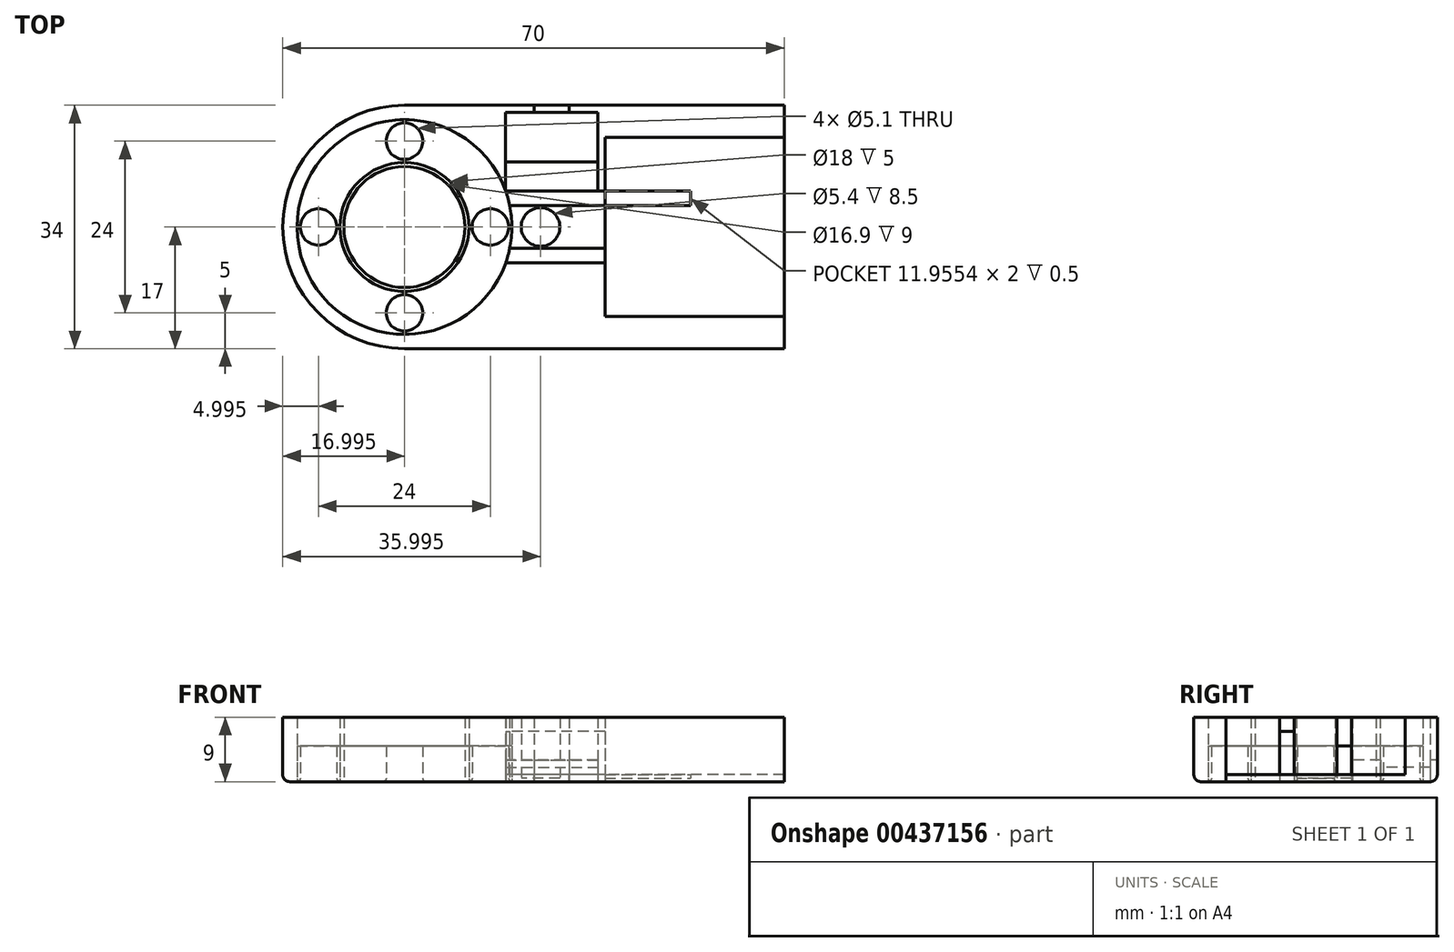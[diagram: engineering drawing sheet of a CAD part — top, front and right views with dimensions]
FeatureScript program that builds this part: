
annotation { "Feature Type Name" : "Feature", "Feature Type Description" : "" }
export const myFeature = defineFeature(function(context is Context, id is Id, definition is map)
    precondition{}
    {
        {
            var Q0;
            Q0=qCreatedBy(makeId("Top.planeOp"),FACE);
            var sketch = newSketch(context, id + "F0", { "sketchPlane" : qUnion([Q0])});
            skPoint(sketch, "E0", {"position": v(-7.91, 0) * mm});
            skPoint(sketch, "E1", {"position": v(33.09, 0) * mm});
            skLineSegment(sketch, "E2", {"start": v(-7.91, 17) * mm, "end": v(45.09, 17) * mm});
            skLineSegment(sketch, "E3", {"start": v(45.09, 17) * mm, "end": v(45.09, -17) * mm});
            skLineSegment(sketch, "E4", {"start": v(45.09, -17) * mm, "end": v(-7.91, -17) * mm});
            skArc(sketch, "E5", {"start": v(-7.91, -17) * mm, "mid": v(-24.91, 0) * mm, "end": v(-7.91, 17) * mm});
            skCircle(sketch, "E6", {"center": v(-7.91, 0) * mm, "radius": 8.45 * mm});
            skLineSegment(sketch, "E7", {"start": v(45.09, 12.5) * mm, "end": v(20.09, 12.5) * mm});
            skLineSegment(sketch, "E8", {"start": v(20.09, 12.5) * mm, "end": v(20.09, -12.5) * mm});
            skLineSegment(sketch, "E9", {"start": v(20.09, -12.5) * mm, "end": v(45.09, -12.5) * mm});
            skCircle(sketch, "E10", {"center": v(-7.91, 0) * mm, "radius": 9 * mm});
            skCircle(sketch, "E11", {"center": v(-7.91, 0) * mm, "radius": 15 * mm});
            skCircle(sketch, "E12", {"center": v(-7.91, 12) * mm, "radius": 2.55 * mm});
            skCircle(sketch, "E13", {"center": v(-7.91, -12) * mm, "radius": 2.55 * mm});
            skCircle(sketch, "E14", {"center": v(4.09, 0) * mm, "radius": 2.55 * mm});
            skCircle(sketch, "E15", {"center": v(-19.91, 0) * mm, "radius": 2.55 * mm});
            skCircle(sketch, "E16", {"center": v(11.09, 0) * mm, "radius": 2.7 * mm});
            skLineSegment(sketch, "E17", {"start": v(20.09, 3) * mm, "end": v(6.78, 3) * mm});
            skLineSegment(sketch, "E18", {"start": v(20.09, 5) * mm, "end": v(6.23, 5) * mm});
            skLineSegment(sketch, "E19", {"start": v(20.09, -3) * mm, "end": v(6.78, -3) * mm});
            skLineSegment(sketch, "E20", {"start": v(20.09, -5) * mm, "end": v(6.23, -5) * mm});
            skLineSegment(sketch, "E21.bottom", {"start": v(6.19, 16) * mm, "end": v(19.09, 16) * mm});
            skLineSegment(sketch, "E21.left", {"start": v(6.19, 16) * mm, "end": v(6.19, 6) * mm});
            skLineSegment(sketch, "E21.right", {"start": v(19.09, 16) * mm, "end": v(19.09, 6) * mm});
            skLineSegment(sketch, "E22", {"start": v(6.19, 9.1) * mm, "end": v(19.09, 9.1) * mm});
            skLineSegment(sketch, "E23", {"start": v(10.19, 17) * mm, "end": v(10.19, 16) * mm});
            skLineSegment(sketch, "E24", {"start": v(15.09, 17) * mm, "end": v(15.09, 16) * mm});
            skLineSegment(sketch, "E25", {"start": v(6.19, 6) * mm, "end": v(6.19, 5) * mm});
            skLineSegment(sketch, "E26", {"start": v(19.09, 6) * mm, "end": v(19.09, 5) * mm});
            skLineSegment(sketch, "E27", {"start": v(20.09, 5) * mm, "end": v(32.04, 5) * mm});
            skLineSegment(sketch, "E28", {"start": v(32.04, 5) * mm, "end": v(32.04, 3) * mm});
            skLineSegment(sketch, "E29", {"start": v(32.04, 3) * mm, "end": v(20.09, 3) * mm});
            skSolve(sketch);
        }
        {
            var Q0;
            {var subQ9=sQuery(id+"F0.wireOp",EDGE,"E4");Q0=makeQuery(id+"F0.imprint","IMPRINT",FACE,{"disambiguationData":[TD([[makeQuery(id+"F0.imprint","IMPRINT",EDGE,{"derivedFrom":subQ9}),-1.0]])]});}
            var Q1;
            {var subQ1=sQuery(id+"F0.wireOp",EDGE,"E7");Q1=makeQuery(id+"F0.imprint","IMPRINT",FACE,{"disambiguationData":[TD([[makeQuery(id+"F0.imprint","IMPRINT",EDGE,{"derivedFrom":subQ1}),-1.0]])]});}
            var Q2;
            Q2=makeQuery(id+"F0.imprint","IMPRINT",FACE,{"disambiguationData":[TD([[makeQuery(id+"F0.imprint","IMPRINT",EDGE,{"derivedFrom":sQuery(id+"F0.wireOp",EDGE,"E16")}),-1.0]])]});
            var Q3;
            Q3=makeQuery(id+"F0.imprint","IMPRINT",FACE,{"disambiguationData":[TD([[makeQuery(id+"F0.imprint","IMPRINT",EDGE,{"derivedFrom":sQuery(id+"F0.wireOp",EDGE,"E6")}),-1.0]])]});
            extrude(context, id + "F1", {"entities" : qUnion([Q0, Q1, Q2, Q3]), "depth" : 9 * mm});
        }
        {
            var Q0;
            {var subQ3=sQuery(id+"F0.wireOp",EDGE,"E7");Q0=makeQuery(id+"F0.imprint","IMPRINT",FACE,{"disambiguationData":[TD([[makeQuery(id+"F0.imprint","IMPRINT",EDGE,{"derivedFrom":subQ3}),1.0]])]});}
            var Q1;
            {var subQ4=sQuery(id+"F0.wireOp",EDGE,"E17");Q1=makeQuery(id+"F0.imprint","IMPRINT",FACE,{"disambiguationData":[TD([[makeQuery(id+"F0.imprint","IMPRINT",EDGE,{"derivedFrom":subQ4}),-1.0]])]});}
            extrude(context, id + "F2", {"entities" : qUnion([Q0, Q1]), "depth" : 1 * mm});
        }
        {
            var Q0;
            {var subQ3=sQuery(id+"F0.wireOp",EDGE,"E22");Q0=makeQuery(id+"F0.imprint","IMPRINT",FACE,{"disambiguationData":[TD([[makeQuery(id+"F0.imprint","IMPRINT",EDGE,{"derivedFrom":subQ3}),1.0]])]});}
            extrude(context, id + "F3", {"entities" : qUnion([Q0]), "depth" : 2 * mm});
        }
        {
            var Q0;
            {var subQ2=sQuery(id+"F0.wireOp",EDGE,"E27");Q0=makeQuery(id+"F0.imprint","IMPRINT",FACE,{"disambiguationData":[TD([[makeQuery(id+"F0.imprint","IMPRINT",EDGE,{"derivedFrom":subQ2}),-1.0]])]});}
            var Q1;
            Q1=makeQuery(id+"F0.imprint","IMPRINT",FACE,{"disambiguationData":[TD([[makeQuery(id+"F0.imprint","IMPRINT",EDGE,{"derivedFrom":sQuery(id+"F0.wireOp",EDGE,"E16")}),1.0]])]});
            extrude(context, id + "F4", {"entities" : qUnion([Q0, Q1]), "operationType" : NewBodyOperationType.ADD, "depth" : 0.5 * mm});
        }
        {
            var Q0;
            {var subQ0=sQuery(id+"F0.wireOp",EDGE,"E19");Q0=makeQuery(id+"F0.imprint","IMPRINT",FACE,{"disambiguationData":[TD([[makeQuery(id+"F0.imprint","IMPRINT",EDGE,{"derivedFrom":subQ0}),1.0]])]});}
            extrude(context, id + "F5", {"entities" : qUnion([Q0]), "depth" : 7 * mm});
        }
        {
            var Q0;
            Q0=makeQuery(id+"F0.imprint","IMPRINT",FACE,{"disambiguationData":[TD([[makeQuery(id+"F0.imprint","IMPRINT",EDGE,{"derivedFrom":sQuery(id+"F0.wireOp",EDGE,"E10")}),-1.0]])]});
            extrude(context, id + "F6", {"entities" : qUnion([Q0]), "depth" : 5 * mm});
        }
        {
            var Q0;
            {var subQ0=sQuery(id+"F0.wireOp",EDGE,"E22");Q0=makeQuery(id+"F0.imprint","IMPRINT",FACE,{"disambiguationData":[TD([[makeQuery(id+"F0.imprint","IMPRINT",EDGE,{"derivedFrom":subQ0}),-1.0]])]});}
            var Q1;
            {var subQ0=sQuery(id+"F0.wireOp",EDGE,"E23");Q1=makeQuery(id+"F0.imprint","IMPRINT",FACE,{"disambiguationData":[TD([[makeQuery(id+"F0.imprint","IMPRINT",EDGE,{"derivedFrom":subQ0}),1.0]])]});}
            extrude(context, id + "F7", {"entities" : qUnion([Q0, Q1]), "depth" : 3 * mm});
        }
        {
            var Q0;
            Q0=makeQuery(id+"F6.opExtrude","CAP_EDGE",EDGE,{"disambiguationData":[OSD([sQuery(id+"F0.wireOp",EDGE,"E15")])],"isStart":true});
            var Q1;
            Q1=makeQuery(id+"F6.opExtrude","CAP_EDGE",EDGE,{"disambiguationData":[OSD([sQuery(id+"F0.wireOp",EDGE,"E13")])],"isStart":true});
            var Q2;
            Q2=makeQuery(id+"F6.opExtrude","CAP_EDGE",EDGE,{"disambiguationData":[OSD([sQuery(id+"F0.wireOp",EDGE,"E14")])],"isStart":true});
            var Q3;
            Q3=makeQuery(id+"F6.opExtrude","CAP_EDGE",EDGE,{"disambiguationData":[OSD([sQuery(id+"F0.wireOp",EDGE,"E12")])],"isStart":true});
            fillet(context, id + "F8", {"entities" : qUnion([Q0, Q1, Q2, Q3]), "radius" : 0.5 * mm, "tangentPropagation" : true, "allowEdgeOverflow" : false});
        }
        {
            var Q0;
            {var subQ0=sQuery(id+"F0.wireOp",EDGE,"E2");Q0=makeQuery(id+"F1.opExtrude","CAP_EDGE",EDGE,{"disambiguationData":[OSD([subQ0]),TDD([makeQuery(id+"F0.imprint","IMPRINT",EDGE,{"disambiguationData":[TD([[makeQuery(id+"F0.imprint","INTERSECT",VERTEX,{"derivedFrom":[subQ0,sQuery(id+"F0.wireOp",EDGE,"E3")]}),1.0]])],"derivedFrom":subQ0})])],"isStart":true});}
            var Q1;
            Q1=makeQuery(id+"F7.opExtrude","CAP_EDGE",EDGE,{"disambiguationData":[OSD([sQuery(id+"F0.wireOp",EDGE,"E2")])],"isStart":true});
            var Q2;
            {var subQ0=sQuery(id+"F0.wireOp",EDGE,"E2");Q2=makeQuery(id+"F1.opExtrude","CAP_EDGE",EDGE,{"disambiguationData":[OSD([subQ0]),TDD([makeQuery(id+"F0.imprint","IMPRINT",EDGE,{"disambiguationData":[TD([[makeQuery(id+"F0.imprint","INTERSECT",VERTEX,{"derivedFrom":[subQ0,sQuery(id+"F0.wireOp",EDGE,"E5")]}),-1.0]])],"derivedFrom":subQ0})])],"isStart":true});}
            fillet(context, id + "F9", {"entities" : qUnion([Q0, Q1, Q2]), "radius" : 1 * mm, "tangentPropagation" : true, "allowEdgeOverflow" : false});
        }
    });
